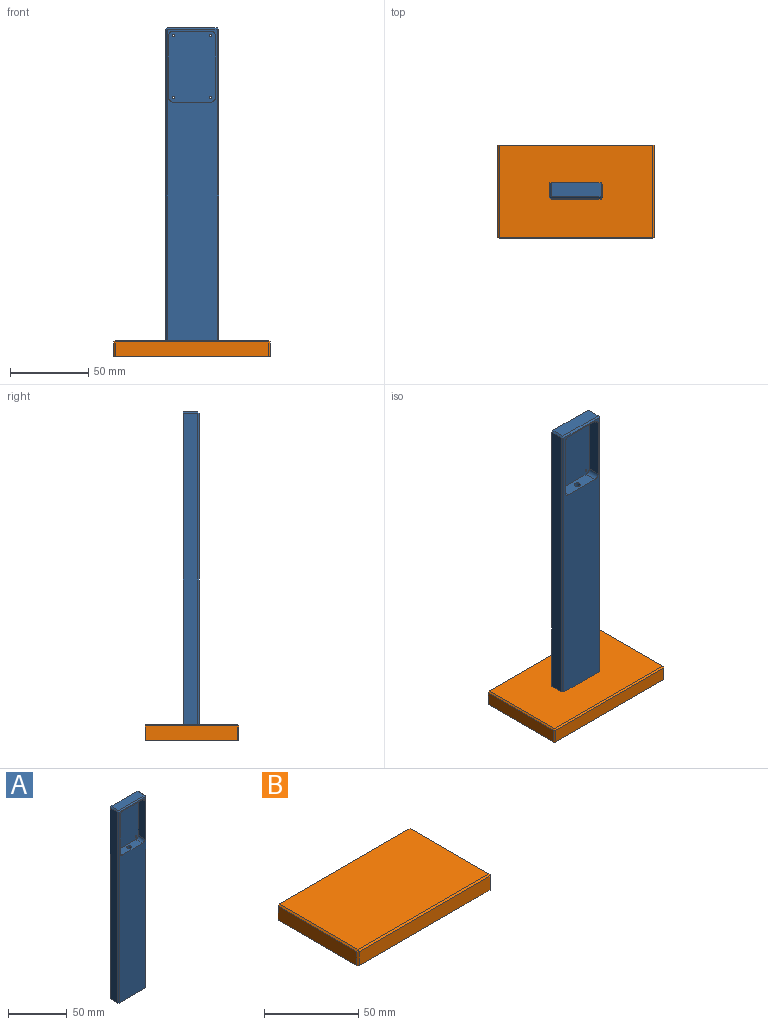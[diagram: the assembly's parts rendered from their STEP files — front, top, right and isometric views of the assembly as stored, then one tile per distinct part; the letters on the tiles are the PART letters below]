
ASSEMBLY  parts=2 mates=2
PART A: 28 faces, bbox 34x10x200 mm
  f0: plane 199x9mm, normal (-1,0,0), area 1791mm2, adj f1,f5,f25,f27
  f1: plane 34x10mm, normal (0,0,-1), area 325.9mm2, adj f0,f2,f4,f5,f15,f20,f22,f25
  f2: plane 199x8mm, normal (1,0,0), area 1592mm2, adj f1,f20,f21,f22
  f3: plane 32x9mm, normal (0,0,1), area 288mm2, adj f5,f21,f24,f27
  f4: plane 199x32mm, normal (0,-1,0), area 5010.7mm2, adj f1,f6,f7,f8,f9,f10,f11,f12
  f5: plane 200x33mm, normal (0,1,0), area 6592.4mm2, adj f0,f1,f3,f16,f17,f18,f19,f20
  f6: cylinder r=3mm len=8mm, axis (0,-1,0), area 37.7mm2, adj f4,f7,f13,f14
  f7: plane 24x8mm, normal (0,0,1), area 179.4mm2, adj f4,f6,f8,f14,f15
  f8: cylinder r=3mm len=8mm, axis (0,-1,0), area 37.7mm2, adj f4,f7,f9,f14
  f9: plane 39.5x8mm, normal (-1,0,0), area 316mm2, adj f4,f8,f10,f14
  f10: cylinder r=3mm len=8mm, axis (0,-1,0), area 37.7mm2, adj f4,f9,f11,f14
  f11: plane 24x8mm, normal (0,0,-1), area 192mm2, adj f4,f10,f12,f14
  f12: cylinder r=3mm len=8mm, axis (0,-1,0), area 37.7mm2, adj f4,f11,f13,f14
  f13: plane 39.5x8mm, normal (1,0,0), area 316mm2, adj f4,f6,f12,f14
  f14: plane 45.5x30mm, normal (0,-1,0), area 1350.2mm2, adj f6,f7,f8,f9,f10,f11,f12,f13
  f15: cylinder r=2mm len=152.5mm, axis (0,0,-1), area 1916.4mm2, adj f1,f7
  f16: cylinder r=0.75mm len=2mm, axis (0,-1,0), area 9.4mm2, adj f5,f14
  f17: cylinder r=0.75mm len=2mm, axis (0,-1,0), area 9.4mm2, adj f5,f14
  f18: cylinder r=0.75mm len=2mm, axis (0,-1,0), area 9.4mm2, adj f5,f14
  f19: cylinder r=0.75mm len=2mm, axis (0,-1,0), area 9.4mm2, adj f5,f14
  f20: plane 200x1mm, normal (0.71,0.71,0), area 282.1mm2, adj f1,f2,f5,f21
  f21: plane 9x1mm, normal (0.71,0,0.71), area 12mm2, adj f2,f3,f20,f23
  f22: plane 199x1mm, normal (0.71,-0.71,0), area 281.4mm2, adj f1,f2,f4,f23
  f23: plane 1x1mm, normal (0.58,-0.58,0.58), area 0.9mm2, adj f21,f22,f24
  f24: plane 32x1mm, normal (0,-0.71,0.71), area 45.3mm2, adj f3,f4,f23,f26
  f25: plane 199x1mm, normal (-0.71,-0.71,0), area 281.4mm2, adj f0,f1,f4,f26
  f26: plane 1x1mm, normal (-0.58,-0.58,0.58), area 0.9mm2, adj f24,f25,f27
  f27: plane 9x1mm, normal (-0.71,0,0.71), area 12.7mm2, adj f0,f3,f5,f26
PART B: 24 faces, bbox 100x60x10 mm
  f0: plane 100x10mm, normal (0,1,0), area 839mm2, adj f1,f3,f4,f5,f6,f9,f14,f15
  f1: plane 59x9mm, normal (-1,0,0), area 531mm2, adj f0,f5,f9,f12
  f2: plane 98x9mm, normal (0,-1,0), area 882mm2, adj f5,f7,f10,f12
  f3: plane 59x9mm, normal (1,0,0), area 531mm2, adj f0,f5,f6,f7
  f4: plane 98x59mm, normal (0,0,1), area 5782mm2, adj f0,f6,f9,f10
  f5: plane 100x60mm, normal (0,0,-1), area 2629.9mm2, adj f0,f1,f2,f3,f7,f12,f13,f14
  f6: plane 59x1mm, normal (0.71,0,0.71), area 83.4mm2, adj f0,f3,f4,f8
  f7: plane 9x1mm, normal (0.71,-0.71,0), area 12.7mm2, adj f2,f3,f5,f8
  f8: plane 1x1mm, normal (0.58,-0.58,0.58), area 0.9mm2, adj f6,f7,f10
  f9: plane 59x1mm, normal (-0.71,0,0.71), area 83.4mm2, adj f0,f1,f4,f11
  f10: plane 98x1mm, normal (0,-0.71,0.71), area 138.6mm2, adj f2,f4,f8,f11
  f11: plane 1x1mm, normal (-0.58,-0.58,0.58), area 0.9mm2, adj f9,f10,f12
  f12: plane 9x1mm, normal (-0.71,-0.71,0), area 12.7mm2, adj f1,f2,f5,f11
  f13: plane 48x8mm, normal (0,-1,0), area 384mm2, adj f5,f14,f22,f23
  f14: plane 10x8mm, normal (1,0,0), area 80mm2, adj f0,f5,f13,f23
  f15: plane 10x8mm, normal (-1,0,0), area 80mm2, adj f0,f5,f16,f23
  f16: cylinder r=6mm len=8mm, axis (0,0,-1), area 75.4mm2, adj f5,f15,f17,f23
  f17: plane 28x8mm, normal (-1,0,0), area 224mm2, adj f5,f16,f18,f23
  f18: cylinder r=6mm len=8mm, axis (0,0,-1), area 75.4mm2, adj f5,f17,f19,f23
  f19: plane 68x8mm, normal (0,1,0), area 544mm2, adj f5,f18,f20,f23
  f20: cylinder r=6mm len=8mm, axis (0,0,-1), area 75.4mm2, adj f5,f19,f21,f23
  f21: plane 28x8mm, normal (1,0,0), area 224mm2, adj f5,f20,f22,f23
  f22: cylinder r=6mm len=8mm, axis (0,0,-1), area 75.4mm2, adj f5,f13,f21,f23
  f23: plane 80x50mm, normal (0,0,-1), area 3369.1mm2, adj f0,f13,f14,f15,f16,f17,f18,f19
PLACE A t=(-71.77,28.05,123.87)mm
PLACE B t=(-94.33,-11.1,-34.01)mm
MATE planar B.f4 <-> A.f1  axis (0,0,1) through (-76.36,23.09,-24.01)mm
MATE parallel A.f1 <-> B.f4  axis (0,0,-1) through (-59.33,23.05,-24.01)mm
